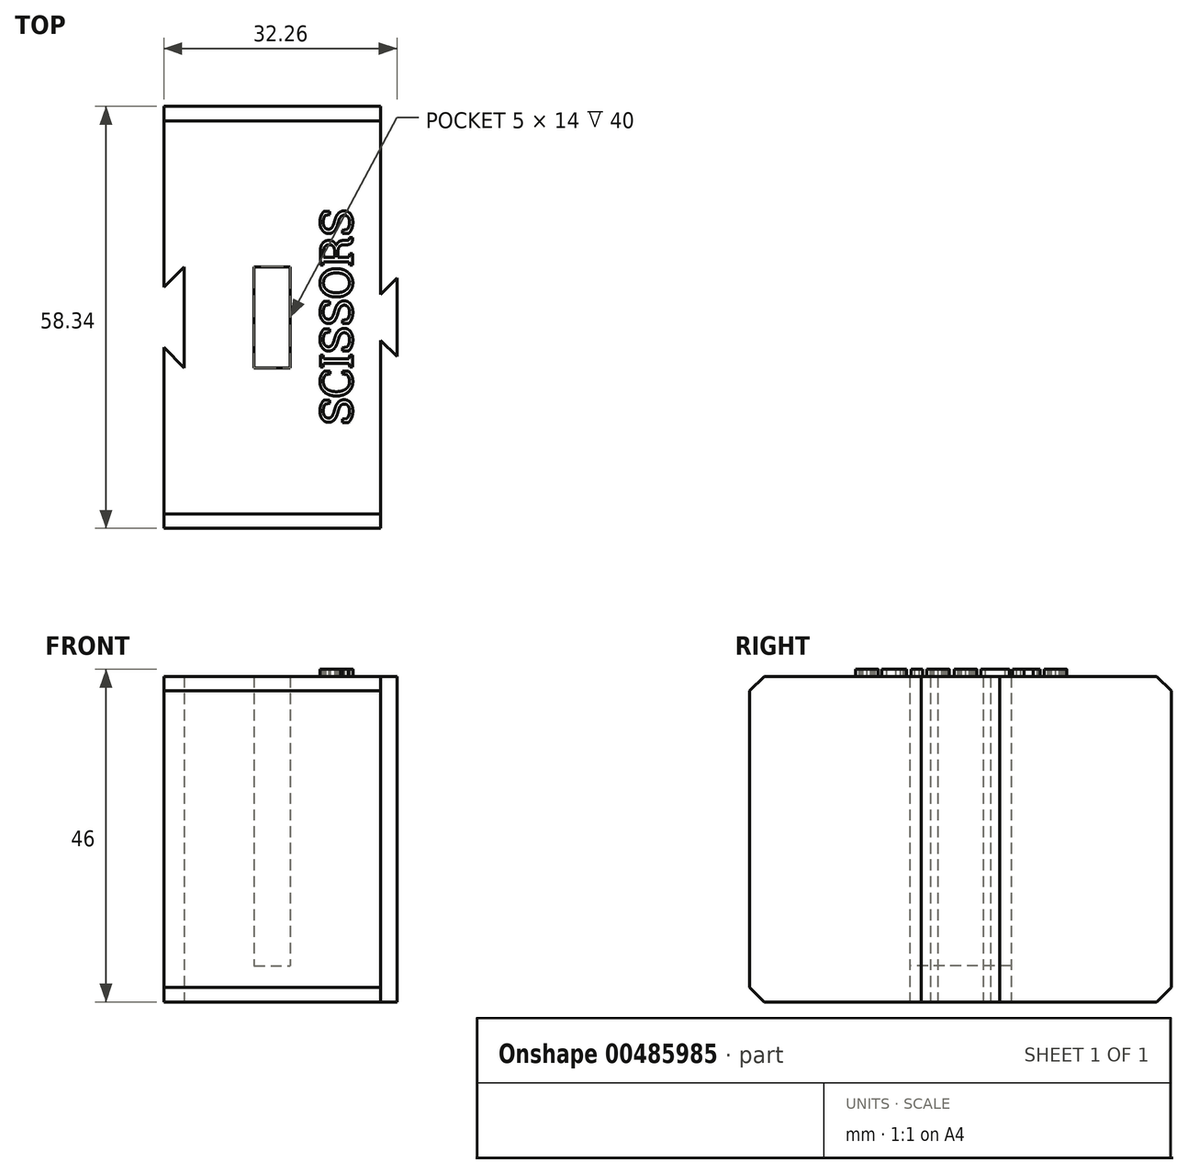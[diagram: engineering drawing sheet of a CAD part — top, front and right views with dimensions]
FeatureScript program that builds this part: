
annotation { "Feature Type Name" : "Feature", "Feature Type Description" : "" }
export const myFeature = defineFeature(function(context is Context, id is Id, definition is map)
    precondition{}
    {
        {
            var Q0;
            Q0=qCreatedBy(makeId("Top.planeOp"),FACE);
            var sketch = newSketch(context, id + "F0", { "sketchPlane" : qUnion([Q0])});
            skLineSegment(sketch, "E0", {"start": v(-15, 4.17) * mm, "end": v(-15, 29.17) * mm});
            skLineSegment(sketch, "E1", {"start": v(-15, 29.17) * mm, "end": v(15, 29.17) * mm});
            skLineSegment(sketch, "E2", {"start": v(15, 29.17) * mm, "end": v(15, 3.17) * mm});
            skLineSegment(sketch, "E3", {"start": v(-15, 4.17) * mm, "end": v(-12.17, 7) * mm});
            skLineSegment(sketch, "E4", {"start": v(-12.17, 7) * mm, "end": v(-12.17, 0) * mm});
            skLineSegment(sketch, "E5", {"start": v(15, 3.17) * mm, "end": v(17.26, 5.43) * mm});
            skLineSegment(sketch, "E6", {"start": v(17.26, 5.43) * mm, "end": v(17.26, -0.57) * mm});
            skLineSegment(sketch, "E7.MirrorCS", {"start": v(-15, -4.17) * mm, "end": v(-12.17, -7) * mm});
            skLineSegment(sketch, "E8.MirrorCS", {"start": v(15, -29.17) * mm, "end": v(15, -3.17) * mm});
            skLineSegment(sketch, "E9.MirrorCS", {"start": v(-12.17, -7) * mm, "end": v(-12.17, 0) * mm});
            skLineSegment(sketch, "E10.MirrorCS", {"start": v(-15, -4.17) * mm, "end": v(-15, -29.17) * mm});
            skLineSegment(sketch, "E11.MirrorCS", {"start": v(17.26, -5.43) * mm, "end": v(17.26, 0.57) * mm});
            skLineSegment(sketch, "E12.MirrorCS", {"start": v(15, -3.17) * mm, "end": v(17.26, -5.43) * mm});
            skLineSegment(sketch, "E13.MirrorCS", {"start": v(-15, -29.17) * mm, "end": v(15, -29.17) * mm});
            skLineSegment(sketch, "E14.bottom", {"start": v(-2.5, 7) * mm, "end": v(2.5, 7) * mm});
            skLineSegment(sketch, "E14.top", {"start": v(-2.5, -7) * mm, "end": v(2.5, -7) * mm});
            skLineSegment(sketch, "E14.left", {"start": v(-2.5, 7) * mm, "end": v(-2.5, -7) * mm});
            skLineSegment(sketch, "E14.right", {"start": v(2.5, 7) * mm, "end": v(2.5, -7) * mm});
            skPoint(sketch, "E14.middle", {"position": v(0, 0) * mm});
            skSolve(sketch);
        }
        {
            var Q0;
            Q0=qSketchRegion(id+"F0",true);
            extrude(context, id + "F1", {"entities" : qUnion([Q0]), "depth" : 40 * mm});
        }
        {
            var Q0;
            Q0=makeQuery(id+"F0.imprint","IMPRINT",FACE,{"disambiguationData":[TD([[makeQuery(id+"F0.imprint","IMPRINT",EDGE,{"derivedFrom":sQuery(id+"F0.wireOp",EDGE,"E0")}),-1.0]])]});
            var Q1;
            Q1=makeQuery(id+"F0.imprint","IMPRINT",FACE,{"disambiguationData":[TD([[makeQuery(id+"F0.imprint","IMPRINT",EDGE,{"derivedFrom":sQuery(id+"F0.wireOp",EDGE,"E14.bottom")}),-1.0]])]});
            extrude(context, id + "F2", {"entities" : qUnion([Q0, Q1]), "operationType" : NewBodyOperationType.ADD, "oppositeDirection" : true, "depth" : 5 * mm});
        }
        {
            var Q0;
            Q0=makeQuery(id+"F2.opExtrude","CAP_EDGE",EDGE,{"disambiguationData":[OSD([sQuery(id+"F0.wireOp",EDGE,"E13.MirrorCS")])],"isStart":false});
            var Q1;
            Q1=makeQuery(id+"F2.opExtrude","CAP_EDGE",EDGE,{"disambiguationData":[OSD([sQuery(id+"F0.wireOp",EDGE,"E1")])],"isStart":false});
            var Q2;
            Q2=makeQuery(id+"F1.opExtrude","CAP_EDGE",EDGE,{"disambiguationData":[OSD([sQuery(id+"F0.wireOp",EDGE,"E13.MirrorCS")])],"isStart":false});
            var Q3;
            Q3=makeQuery(id+"F1.opExtrude","CAP_EDGE",EDGE,{"disambiguationData":[OSD([sQuery(id+"F0.wireOp",EDGE,"E1")])],"isStart":false});
            chamfer(context, id + "F3", {"entities" : qUnion([Q0, Q1, Q2, Q3]), "width" : 2 * mm, "tangentPropagation" : true});
        }
        {
            var Q0;
            Q0=makeQuery(id+"F1.opExtrude","CAP_FACE",FACE,{"disambiguationData":[OSD([sQuery(id+"F0.wireOp",EDGE,"E0"),sQuery(id+"F0.wireOp",EDGE,"E1"),sQuery(id+"F0.wireOp",EDGE,"E2"),sQuery(id+"F0.wireOp",EDGE,"E3"),sQuery(id+"F0.wireOp",EDGE,"E4"),sQuery(id+"F0.wireOp",EDGE,"E5"),sQuery(id+"F0.wireOp",EDGE,"E6"),sQuery(id+"F0.wireOp",EDGE,"E7.MirrorCS"),sQuery(id+"F0.wireOp",EDGE,"E8.MirrorCS"),sQuery(id+"F0.wireOp",EDGE,"E9.MirrorCS"),sQuery(id+"F0.wireOp",EDGE,"E10.MirrorCS"),sQuery(id+"F0.wireOp",EDGE,"E11.MirrorCS"),sQuery(id+"F0.wireOp",EDGE,"E12.MirrorCS"),sQuery(id+"F0.wireOp",EDGE,"E13.MirrorCS"),sQuery(id+"F0.wireOp",EDGE,"E14.bottom"),sQuery(id+"F0.wireOp",EDGE,"E14.top"),sQuery(id+"F0.wireOp",EDGE,"E14.left"),sQuery(id+"F0.wireOp",EDGE,"E14.right")])],"isStart":false});
            var sketch = newSketch(context, id + "F4", { "sketchPlane" : qUnion([Q0])});
            skText(sketch, "E15", { "text": "SCISSORS", "fontName": "RobotoSlab-Regular.ttf"});
            const initialGuessF4  = {"E15": [0.0111, -0.0149, 0, 1, 0.0045]};
            skSetInitialGuess(sketch, initialGuessF4);
            skSolve(sketch);
        }
        {
            var Q0;
            Q0=qSketchRegion(id+"F4",true);
            extrude(context, id + "F5", {"entities" : qUnion([Q0]), "operationType" : NewBodyOperationType.ADD, "depth" : 1 * mm});
        }
    });
